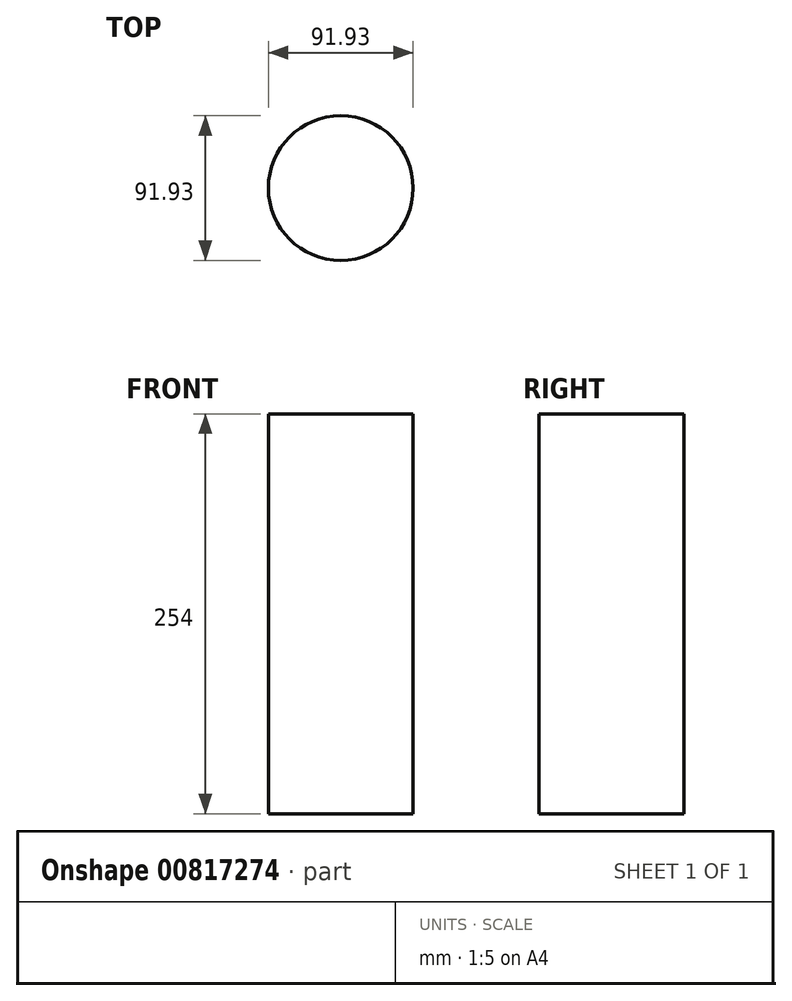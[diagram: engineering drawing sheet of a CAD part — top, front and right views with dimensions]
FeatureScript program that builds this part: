
annotation { "Feature Type Name" : "Feature", "Feature Type Description" : "" }
export const myFeature = defineFeature(function(context is Context, id is Id, definition is map)
    precondition{}
    {
        {
            var Q0;
            Q0=qCreatedBy(makeId("Top.planeOp"),FACE);
            var sketch = newSketch(context, id + "F0", { "sketchPlane" : qUnion([Q0])});
            skCircle(sketch, "E0", {"center": v(-25.19, -3.81) * mm, "radius": 45.97 * mm});
            skPoint(sketch, "E0.first.point", {"position": v(-40.2, 39.63) * mm});
            skPoint(sketch, "E0.second.point", {"position": v(-38.1, -47.93) * mm});
            skPoint(sketch, "E0.third.point", {"position": v(9.7, 26.1) * mm});
            skCircle(sketch, "E1", {"center": v(-25.19, -3.81) * mm, "radius": 25.47 * mm});
            skPoint(sketch, "E1.first.point", {"position": v(-36.03, 19.24) * mm});
            skPoint(sketch, "E1.second.point", {"position": v(0, 0) * mm});
            skPoint(sketch, "E1.third.point", {"position": v(-32.88, -28.1) * mm});
            skSolve(sketch);
        }
        {
            var Q0;
            Q0=sQuery(id+"F0.wireOp",EDGE,"E0");
            extrude(context, id + "F1", {"bodyType" : ToolBodyType.SURFACE, "surfaceEntities" : qUnion([Q0]), "depth" : 254 * mm, "offsetDistance" : 25.4 * mm});
        }
    });
